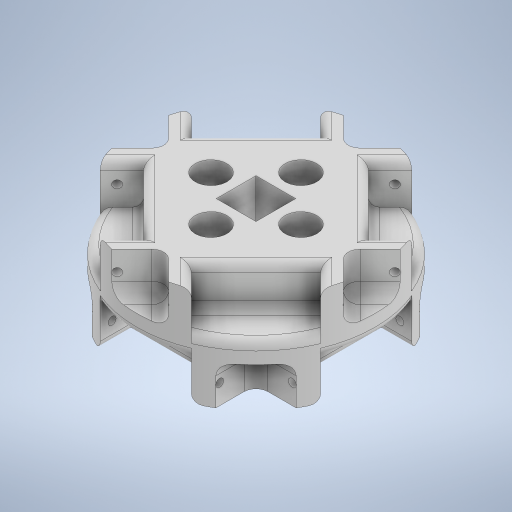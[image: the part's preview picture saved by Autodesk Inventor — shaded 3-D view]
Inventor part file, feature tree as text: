
AUTODESK INVENTOR PART (.ipt)
format: ipt  version: 2024.2 (Build 282272000, 272)  size: 612,864 bytes
history: native  units: mm
features: extrude x9, sketch x9, pattern_circular x5, fillet x4
ambient origin geometry x8: Origin, YZ Plane, XZ Plane, XY Plane, X Axis, Y Axis, Z Axis, Center Point
bodies: Solid1 (feature_tree)
feature tree (27):
  extrude  "Extrusion1"  Depth=25.0mm TaperAngle=0.0deg
  extrude  "Extrusion2"  TaperAngle=45.0deg  [1 undecoded]
  extrude  "Extrusion3"  Depth=10.0mm TaperAngle=0.0deg
  extrude  "Extrusion4"  Depth=10.0mm
  fillet  "Fillet1"  Radius=10.0mm
  pattern_circular  "Circular Pattern2"  Count=4 Angle=360.0deg
  extrude  "Extrusion5"  Depth=10.0mm
  fillet  "Fillet2"  Radius=2.0mm
  pattern_circular  "Circular Pattern3"  [2 undecoded]
  extrude  "Extrusion6"  Depth=2.0mm
  extrude  "Extrusion7"  Depth=10.0mm TaperAngle=360.0deg
  fillet  "Fillet3"  Radius=10.0mm
  pattern_circular  "Circular Pattern4"  [2 undecoded]
  extrude  "Extrusion8"  TaperAngle=0.0deg  [1 undecoded]
  fillet  "Fillet4"  Radius=3.0mm
  pattern_circular  "Circular Pattern5"  Angle=90.0deg  [1 undecoded]
  extrude  "Extrusion9"  TaperAngle=45.0deg  [1 undecoded]
  pattern_circular  "Circular Pattern6"  Count=2  [1 undecoded]
  sketch  "Sketch1"  dims[d0=60.0mm d1=25.0mm d2=0.0mm]
  sketch  "Sketch2"  dims[d3=23.0mm d5=45.0deg]
  sketch  "Sketch3"  dims[d6=10.0mm d7=10.0mm d8=0.0mm]
  sketch  "Sketch4"  dims[d12=23.0mm d14=10.0mm d15=10.0mm d16=0.0mm]
  sketch  "Sketch5"  dims[d17=5.0mm]
  sketch  "Sketch6"  dims[d18=3.0mm]
  sketch  "Sketch7"  dims[d19=2.0mm]
  sketch  "Sketch8"  dims[d20=0.0mm d21=0.0mm]
  sketch  "Sketch9"  dims[d22=2.0mm d23=40.0mm d24=360.0deg d26=5.0mm d28=2.0mm d29=0.0mm d30=0.0mm d31=2.0mm d32=40.0mm d33=360.0deg d35=10.0mm d36=10.0mm d37=0.0mm d38=0.0mm d39=3.0mm d40=90.0deg d41=45.0deg d42=20.0mm d43=10.0mm d44=0.0mm d45=3.0mm d46=40.0mm d47=360.0deg d49=20.0mm d50=20.0mm d51=10.0mm d52=0.0mm d53=3.0mm d54=40.0mm d55=360.0deg d57=8.0mm d58=10.0mm d59=10.0mm d60=0.0mm d61=0.0mm d62=40.0mm d63=360.0deg]
note: 9 required parameter values undecoded (feature->parameter linkage not recoverable at this tier; creation-order binding heuristic only, values carry confidence <= 0.55)
